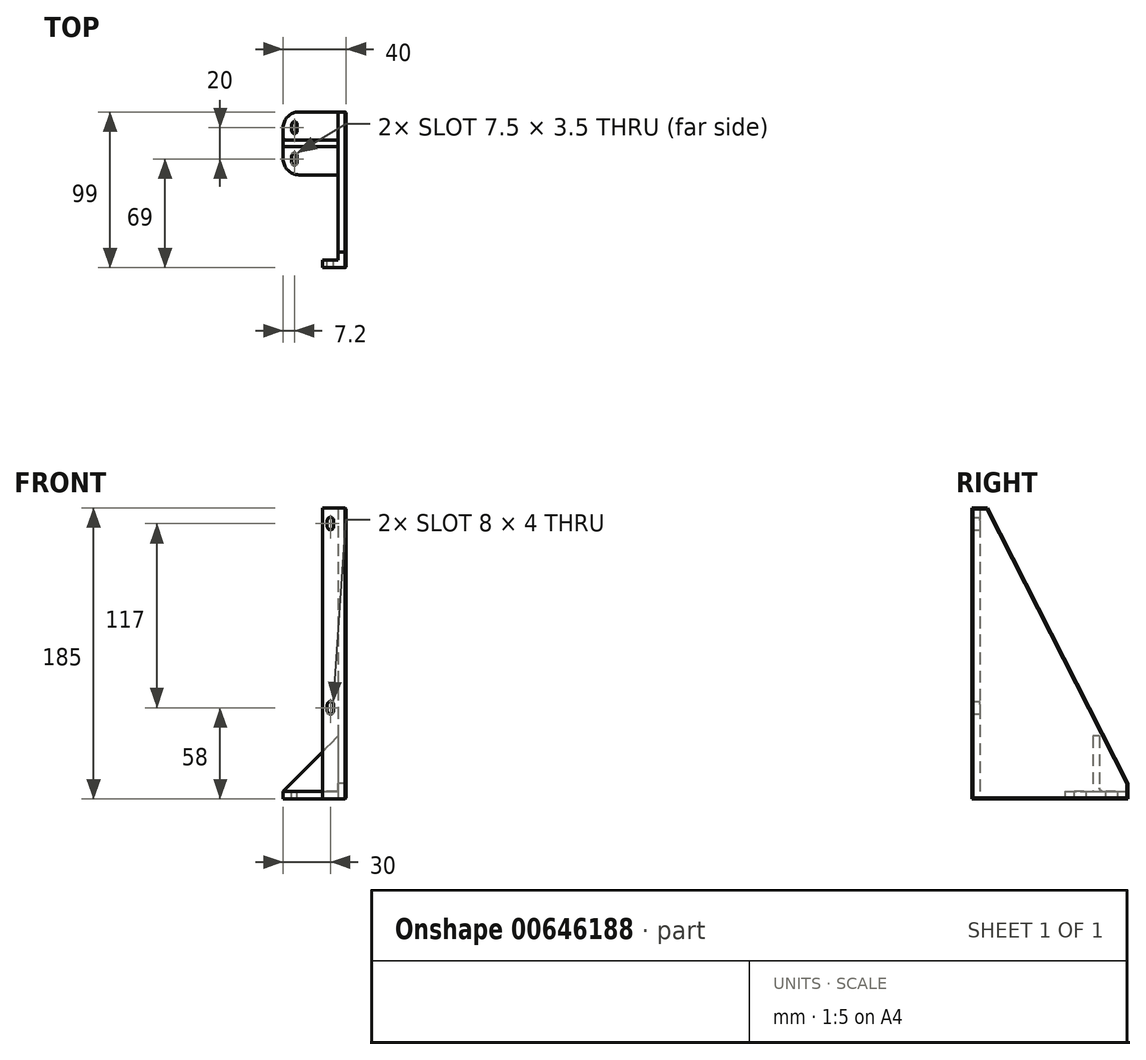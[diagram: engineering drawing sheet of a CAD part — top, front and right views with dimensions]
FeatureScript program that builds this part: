
annotation { "Feature Type Name" : "Feature", "Feature Type Description" : "" }
export const myFeature = defineFeature(function(context is Context, id is Id, definition is map)
    precondition{}
    {
        {
            var Q0;
            Q0=qCreatedBy(makeId("Right.planeOp"),FACE);
            var sketch = newSketch(context, id + "F0", { "sketchPlane" : qUnion([Q0])});
            skLineSegment(sketch, "E0", {"start": v(0, 0) * mm, "end": v(0, 185) * mm});
            skLineSegment(sketch, "E1", {"start": v(0, 0) * mm, "end": v(99, 0) * mm});
            skLineSegment(sketch, "E2", {"start": v(0, 185) * mm, "end": v(10, 185) * mm});
            skLineSegment(sketch, "E3", {"start": v(99, 0) * mm, "end": v(99, 10) * mm});
            skLineSegment(sketch, "E4", {"start": v(10, 185) * mm, "end": v(99, 10) * mm});
            skLineSegment(sketch, "E5", {"start": v(5, 185) * mm, "end": v(5, 5) * mm});
            skPoint(sketch, "E5.endSnap0", {"position": v(99, 5) * mm});
            skLineSegment(sketch, "E6", {"start": v(5, 5) * mm, "end": v(99, 5) * mm});
            skLineSegment(sketch, "E7", {"start": v(69, 5) * mm, "end": v(69, 0) * mm, "construction": true});
            skLineSegment(sketch, "E8", {"start": v(89, 5) * mm, "end": v(89, 0) * mm, "construction": true});
            skLineSegment(sketch, "E9", {"start": v(59, 5) * mm, "end": v(59, 0) * mm});
            skPoint(sketch, "E9.endSnap0", {"position": v(49.5, 0) * mm});
            skLineSegment(sketch, "E10", {"start": v(5, 5) * mm, "end": v(5, 0) * mm});
            skLineSegment(sketch, "E11", {"start": v(5, 58) * mm, "end": v(0, 58) * mm, "construction": true});
            skLineSegment(sketch, "E12", {"start": v(5, 175) * mm, "end": v(0, 175) * mm, "construction": true});
            skSolve(sketch);
        }
        {
            var Q0;
            Q0 = qSketchRegion(id + "F0", true);
            extrude(context, id + "F1", {"entities" : qUnion([Q0]), "depth" : 5 * mm, "offsetDistance" : 25 * mm});
        }
        {
            var Q0;
            {var subQ2=sQuery(id+"F0.wireOp",EDGE,"E0");Q0=makeQuery(id+"F0.imprint","IMPRINT",FACE,{"disambiguationData":[TD([[makeQuery(id+"F0.imprint","IMPRINT",EDGE,{"derivedFrom":subQ2}),-1.0]])]});}
            extrude(context, id + "F2", {"entities" : qUnion([Q0]), "operationType" : NewBodyOperationType.ADD, "oppositeDirection" : true, "depth" : 10 * mm, "offsetDistance" : 25 * mm});
        }
        {
            var Q0;
            {var subQ3=sQuery(id+"F0.wireOp",EDGE,"E9");Q0=makeQuery(id+"F0.imprint","IMPRINT",FACE,{"disambiguationData":[TD([[makeQuery(id+"F0.imprint","IMPRINT",EDGE,{"derivedFrom":subQ3}),1.0]])]});}
            extrude(context, id + "F3", {"entities" : qUnion([Q0]), "operationType" : NewBodyOperationType.ADD, "oppositeDirection" : true, "depth" : 35 * mm, "offsetDistance" : 25 * mm});
        }
        {
            var Q0;
            Q0=makeQuery(id+"F3.opExtrude","SWEPT_FACE",FACE,{"disambiguationData":[OSD([sQuery(id+"F0.wireOp",EDGE,"E6")])]});
            var sketch = newSketch(context, id + "F4", { "sketchPlane" : qUnion([Q0])});
            skLineSegment(sketch, "E13", {"start": v(0, 89) * mm, "end": v(-35, 89) * mm, "construction": true});
            skLineSegment(sketch, "E14", {"start": v(0, 69) * mm, "end": v(-35, 69) * mm, "construction": true});
            skLineSegment(sketch, "E15", {"start": v(-5, 99) * mm, "end": v(-5, 59) * mm, "construction": true});
            skPoint(sketch, "E16", {"position": v(-27.8, 89) * mm});
            skPoint(sketch, "E17", {"position": v(-27.8, 69) * mm});
            skCircle(sketch, "E18", {"center": v(-27.8, 89) * mm, "radius": 1.75 * mm, "construction": true});
            skCircle(sketch, "E19", {"center": v(-27.8, 69) * mm, "radius": 1.75 * mm, "construction": true});
            skArc(sketch, "E20", {"start": v(-26.05, 91) * mm, "mid": v(-27.8, 92.75) * mm, "end": v(-29.55, 91) * mm});
            skLineSegment(sketch, "E21", {"start": v(-26.05, 91) * mm, "end": v(-26.05, 89) * mm});
            skLineSegment(sketch, "E22", {"start": v(-29.55, 91) * mm, "end": v(-29.55, 89) * mm});
            skLineSegment(sketch, "E23.MirrorCS", {"start": v(-26.05, 87) * mm, "end": v(-26.05, 89) * mm});
            skArc(sketch, "E24.MirrorCS", {"start": v(-26.05, 87) * mm, "mid": v(-27.8, 85.25) * mm, "end": v(-29.55, 87) * mm});
            skLineSegment(sketch, "E25.MirrorCS", {"start": v(-29.55, 87) * mm, "end": v(-29.55, 89) * mm});
            skArc(sketch, "E26", {"start": v(-26.05, 71) * mm, "mid": v(-27.8, 72.75) * mm, "end": v(-29.55, 71) * mm});
            skLineSegment(sketch, "E27", {"start": v(-26.05, 71) * mm, "end": v(-26.05, 69) * mm});
            skLineSegment(sketch, "E28", {"start": v(-29.55, 71) * mm, "end": v(-29.55, 69) * mm});
            skLineSegment(sketch, "E29.MirrorCS", {"start": v(-26.05, 67) * mm, "end": v(-26.05, 69) * mm});
            skArc(sketch, "E30.MirrorCS", {"start": v(-26.05, 67) * mm, "mid": v(-27.8, 65.25) * mm, "end": v(-29.55, 67) * mm});
            skLineSegment(sketch, "E31.MirrorCS", {"start": v(-29.55, 67) * mm, "end": v(-29.55, 69) * mm});
            skLineSegment(sketch, "E32", {"start": v(0, 79) * mm, "end": v(-35, 79) * mm, "construction": true});
            skLineSegment(sketch, "E33", {"start": v(0, 81) * mm, "end": v(-35, 81) * mm});
            skLineSegment(sketch, "E34.MirrorCS", {"start": v(0, 77) * mm, "end": v(-35, 77) * mm});
            skSolve(sketch);
        }
        {
            var Q0;
            Q0=makeQuery(id+"F4.imprint","IMPRINT",FACE,{"disambiguationData":[TD([[makeQuery(id+"F4.imprint","IMPRINT",EDGE,{"derivedFrom":sQuery(id+"F4.wireOp",EDGE,"E26")}),1.0]])]});
            var Q1;
            Q1=makeQuery(id+"F4.imprint","IMPRINT",FACE,{"disambiguationData":[TD([[makeQuery(id+"F4.imprint","IMPRINT",EDGE,{"derivedFrom":sQuery(id+"F4.wireOp",EDGE,"E20")}),1.0]])]});
            extrude(context, id + "F5", {"entities" : qUnion([Q0, Q1]), "operationType" : NewBodyOperationType.REMOVE, "endBound" : BoundingType.THROUGH_ALL, "oppositeDirection" : true, "depth" : 25 * mm, "offsetDistance" : 25 * mm});
        }
        {
            var Q0;
            Q0=makeQuery(id+"F2.opExtrude","SWEPT_FACE",FACE,{"disambiguationData":[OSD([sQuery(id+"F0.wireOp",EDGE,"E5"),sQuery(id+"F0.wireOp",EDGE,"E10")])]});
            var sketch = newSketch(context, id + "F6", { "sketchPlane" : qUnion([Q0])});
            skLineSegment(sketch, "E35", {"start": v(0, 175) * mm, "end": v(10, 175) * mm, "construction": true});
            skLineSegment(sketch, "E36", {"start": v(0, 58) * mm, "end": v(10, 58) * mm, "construction": true});
            skPoint(sketch, "E37", {"position": v(5, 58) * mm});
            skPoint(sketch, "E38", {"position": v(5, 175) * mm});
            skCircle(sketch, "E39", {"center": v(5, 175) * mm, "radius": 2 * mm, "construction": true});
            skArc(sketch, "E40", {"start": v(7, 177) * mm, "mid": v(5, 179) * mm, "end": v(3, 177) * mm});
            skLineSegment(sketch, "E41", {"start": v(7, 177) * mm, "end": v(7, 175) * mm});
            skLineSegment(sketch, "E42", {"start": v(3, 177) * mm, "end": v(3, 175) * mm});
            skLineSegment(sketch, "E43.MirrorCS", {"start": v(7, 173) * mm, "end": v(7, 175) * mm});
            skArc(sketch, "E44.MirrorCS", {"start": v(7, 173) * mm, "mid": v(5, 171) * mm, "end": v(3, 173) * mm});
            skLineSegment(sketch, "E45.MirrorCS", {"start": v(3, 173) * mm, "end": v(3, 175) * mm});
            skCircle(sketch, "E46", {"center": v(5, 58) * mm, "radius": 2 * mm, "construction": true});
            skArc(sketch, "E47", {"start": v(7, 60) * mm, "mid": v(5, 62) * mm, "end": v(3, 60) * mm});
            skLineSegment(sketch, "E48", {"start": v(7, 60) * mm, "end": v(7, 58) * mm});
            skLineSegment(sketch, "E49", {"start": v(3, 60) * mm, "end": v(3, 58) * mm});
            skArc(sketch, "E50.MirrorCS", {"start": v(7, 56) * mm, "mid": v(5, 54) * mm, "end": v(3, 56) * mm});
            skLineSegment(sketch, "E51.MirrorCS", {"start": v(7, 56) * mm, "end": v(7, 58) * mm});
            skLineSegment(sketch, "E52.MirrorCS", {"start": v(3, 56) * mm, "end": v(3, 58) * mm});
            skSolve(sketch);
        }
        {
            var Q0;
            Q0=makeQuery(id+"F6.imprint","IMPRINT",FACE,{"disambiguationData":[TD([[makeQuery(id+"F6.imprint","IMPRINT",EDGE,{"derivedFrom":sQuery(id+"F6.wireOp",EDGE,"E47")}),1.0]])]});
            var Q1;
            Q1=makeQuery(id+"F6.imprint","IMPRINT",FACE,{"disambiguationData":[TD([[makeQuery(id+"F6.imprint","IMPRINT",EDGE,{"derivedFrom":sQuery(id+"F6.wireOp",EDGE,"E40")}),1.0]])]});
            extrude(context, id + "F7", {"entities" : qUnion([Q0, Q1]), "operationType" : NewBodyOperationType.REMOVE, "endBound" : BoundingType.THROUGH_ALL, "oppositeDirection" : true, "depth" : 25 * mm, "offsetDistance" : 25 * mm});
        }
        {
            var Q0;
            {var subQ0=sQuery(id+"F4.wireOp",EDGE,"E33");Q0=makeQuery(id+"F4.imprint","IMPRINT",FACE,{"disambiguationData":[TD([[makeQuery(id+"F4.imprint","IMPRINT",EDGE,{"derivedFrom":subQ0}),1.0]])]});}
            var Q1;
            Q1=makeQuery(id+"F1.opExtrude","SWEPT_FACE",FACE,{"disambiguationData":[OSD([sQuery(id+"F0.wireOp",EDGE,"E4")])]});
            extrude(context, id + "F8", {"entities" : qUnion([Q0]), "operationType" : NewBodyOperationType.ADD, "depth" : 40 * mm, "endBoundEntityFace" : qUnion([Q1]), "offsetDistance" : 25 * mm});
        }
        {
            var Q0;
            {var subQ0=sQuery(id+"F0.wireOp",EDGE,"E6");var subQ1=makeQuery(id+"F3.opExtrude","CAP_EDGE",EDGE,{"disambiguationData":[OSD([subQ0])],"isStart":false});Q0=makeQuery(id+"F8.opExtrude","CAP_EDGE",EDGE,{"disambiguationData":[OSD([subQ0]),TDD([makeQuery(id+"F4.imprint","IMPRINT",EDGE,{"disambiguationData":[TD([[makeQuery(id+"F4.imprint","INTERSECT",VERTEX,{"derivedFrom":[subQ1,sQuery(id+"F4.wireOp",EDGE,"E33")]}),1.0]])],"derivedFrom":subQ1})])],"isStart":false});}
            chamfer(context, id + "F9", {"entities" : qUnion([Q0]), "width" : 40 * mm, "tangentPropagation" : true});
        }
        {
            var Q0;
            Q0=makeQuery(id+"F8.opExtrude","CAP_EDGE",EDGE,{"disambiguationData":[OSD([sQuery(id+"F4.wireOp",EDGE,"E34.MirrorCS")])],"isStart":true});
            var Q1;
            {var subQ0=sQuery(id+"F4.wireOp",EDGE,"E34.MirrorCS");var subQ1=sQuery(id+"F0.wireOp",EDGE,"E6");Q1=makeQuery(id+"F8.opExtrude","SWEPT_EDGE",EDGE,{"disambiguationData":[OSD([subQ1,subQ0]),TDD([makeQuery(id+"F4.imprint","INTERSECT",VERTEX,{"derivedFrom":[makeQuery(id+"F3.opExtrude","CAP_EDGE",EDGE,{"disambiguationData":[OSD([subQ1])],"isStart":true}),subQ0]})])]});}
            var Q2;
            {var subQ0=sQuery(id+"F4.wireOp",EDGE,"E33");var subQ1=sQuery(id+"F0.wireOp",EDGE,"E6");Q2=makeQuery(id+"F8.opExtrude","SWEPT_EDGE",EDGE,{"disambiguationData":[OSD([subQ1,subQ0]),TDD([makeQuery(id+"F4.imprint","INTERSECT",VERTEX,{"derivedFrom":[makeQuery(id+"F3.opExtrude","CAP_EDGE",EDGE,{"disambiguationData":[OSD([subQ1])],"isStart":true}),subQ0]})])]});}
            var Q3;
            Q3=makeQuery(id+"F8.opExtrude","CAP_EDGE",EDGE,{"disambiguationData":[OSD([sQuery(id+"F4.wireOp",EDGE,"E33")])],"isStart":true});
            var Q4;
            {var subQ0=sQuery(id+"F0.wireOp",EDGE,"E6");Q4=makeQuery(id+"F8.boolean.opBoolean","SPLIT",EDGE,{"disambiguationData":[TD([makeQuery(id+"F3.opExtrude","SWEPT_FACE",FACE,{"disambiguationData":[OSD([sQuery(id+"F0.wireOp",EDGE,"E9")])]})])],"derivedFrom":makeQuery(id+"F3.opExtrude","CAP_EDGE",EDGE,{"disambiguationData":[OSD([subQ0])],"isStart":true})});}
            var Q5;
            {var subQ0=sQuery(id+"F0.wireOp",EDGE,"E6");var subQ1=sQuery(id+"F0.wireOp",EDGE,"E3");Q5=makeQuery(id+"F8.boolean.opBoolean","SPLIT",EDGE,{"disambiguationData":[TD([makeQuery(id+"F1.opExtrude","SWEPT_FACE",FACE,{"disambiguationData":[OSD([subQ1])]})])],"derivedFrom":makeQuery(id+"F3.opExtrude","CAP_EDGE",EDGE,{"disambiguationData":[OSD([subQ0])],"isStart":true})});}
            fillet(context, id + "F10", {"entities" : qUnion([Q0, Q1, Q2, Q3, Q4, Q5]), "radius" : 2 * mm, "tangentPropagation" : true, "allowEdgeOverflow" : false});
        }
        {
            var Q0;
            Q0=makeQuery(id+"F3.opExtrude","CAP_EDGE",EDGE,{"disambiguationData":[OSD([sQuery(id+"F0.wireOp",EDGE,"E9")])],"isStart":false});
            var Q1;
            Q1=makeQuery(id+"F3.opExtrude","CAP_EDGE",EDGE,{"disambiguationData":[OSD([sQuery(id+"F0.wireOp",EDGE,"E3")])],"isStart":false});
            fillet(context, id + "F11", {"entities" : qUnion([Q0, Q1]), "radius" : 10 * mm, "tangentPropagation" : true, "allowEdgeOverflow" : false});
        }
        {
            var Q0;
            Q0=makeQuery(id+"F1.opExtrude","CAP_FACE",FACE,{"disambiguationData":[OSD([sQuery(id+"F0.wireOp",EDGE,"E0"),sQuery(id+"F0.wireOp",EDGE,"E1"),sQuery(id+"F0.wireOp",EDGE,"E2"),sQuery(id+"F0.wireOp",EDGE,"E3"),sQuery(id+"F0.wireOp",EDGE,"E4")])],"isStart":false});
            chamfer(context, id + "F12", {"entities" : qUnion([Q0]), "width" : .6 * mm, "tangentPropagation" : true});
        }
    });
